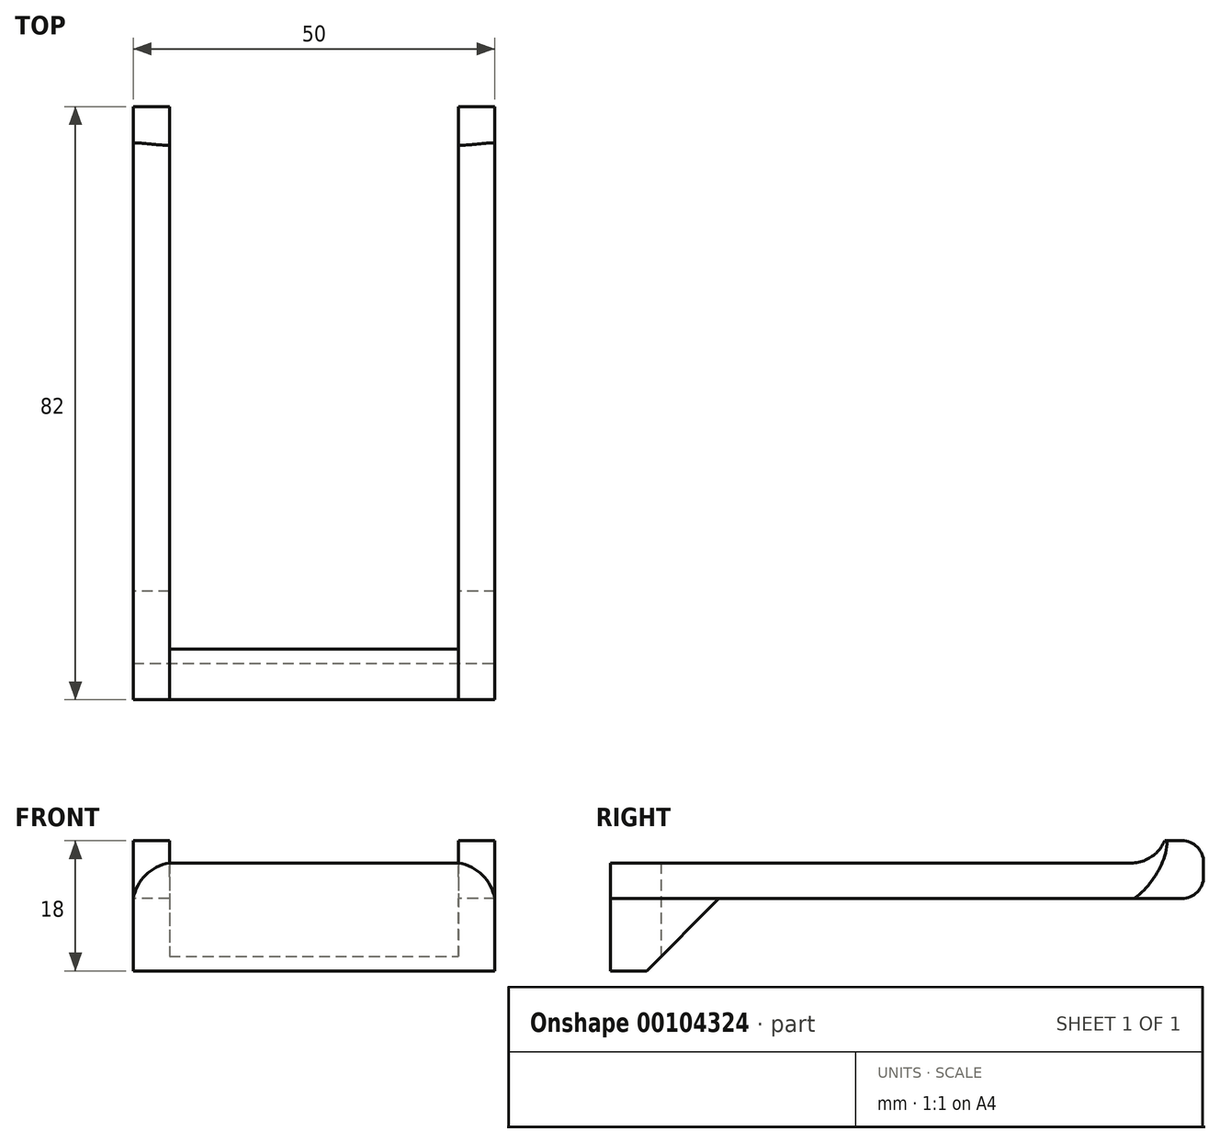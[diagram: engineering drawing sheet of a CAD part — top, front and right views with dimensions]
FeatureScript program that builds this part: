
annotation { "Feature Type Name" : "Feature", "Feature Type Description" : "" }
export const myFeature = defineFeature(function(context is Context, id is Id, definition is map)
    precondition{}
    {
        {
            var Q0;
            Q0=qCreatedBy(makeId("Front.planeOp"),FACE);
            var sketch = newSketch(context, id + "F0", { "sketchPlane" : qUnion([Q0])});
            skLineSegment(sketch, "E0.bottom", {"start": v(0, 0) * mm, "end": v(-5, 0) * mm});
            skLineSegment(sketch, "E0.top", {"start": v(0, 5) * mm, "end": v(-5, 5) * mm});
            skLineSegment(sketch, "E0.left", {"start": v(0, 0) * mm, "end": v(0, 5) * mm});
            skLineSegment(sketch, "E0.right", {"start": v(-5, 0) * mm, "end": v(-5, 5) * mm});
            skLineSegment(sketch, "E1", {"start": v(0, 5) * mm, "end": v(0, 8) * mm});
            skLineSegment(sketch, "E2", {"start": v(0, 8) * mm, "end": v(-5, 8) * mm});
            skLineSegment(sketch, "E3", {"start": v(-5, 8) * mm, "end": v(-5, 5) * mm});
            skSolve(sketch);
        }
        {
            var Q0;
            Q0=makeQuery(id+"F0.imprint","IMPRINT",FACE,{"disambiguationData":[TD([[makeQuery(id+"F0.imprint","IMPRINT",EDGE,{"derivedFrom":sQuery(id+"F0.wireOp",EDGE,"E0.bottom")}),-1.0]])]});
            extrude(context, id + "F1", {"entities" : qUnion([Q0]), "depth" : 82 * mm});
        }
        {
            var Q0;
            Q0=makeQuery(id+"F0.imprint","IMPRINT",FACE,{"disambiguationData":[TD([[makeQuery(id+"F0.imprint","IMPRINT",EDGE,{"derivedFrom":sQuery(id+"F0.wireOp",EDGE,"E0.top")}),-1.0]])]});
            extrude(context, id + "F2", {"entities" : qUnion([Q0]), "operationType" : NewBodyOperationType.ADD, "depth" : 5 * mm});
        }
        {
            var Q0;
            Q0=makeQuery(id+"F1.opExtrude","SWEPT_EDGE",EDGE,{"disambiguationData":[OSD([sQuery(id+"F0.wireOp",EDGE,"E0.top"),sQuery(id+"F0.wireOp",EDGE,"E0.right"),sQuery(id+"F0.wireOp",EDGE,"E3")])]});
            fillet(context, id + "F3", {"entities" : qUnion([Q0]), "radius" : 6.1 * mm, "tangentPropagation" : true, "allowEdgeOverflow" : false});
        }
        {
            var Q0;
            {var subQ0=sQuery(id+"F0.wireOp",EDGE,"E3");var subQ1=sQuery(id+"F0.wireOp",EDGE,"E0.top");Q0=makeQuery(id+"F3.opFillet","BLEND_EDGE",EDGE,{"blendedFrom":[makeQuery(id+"F1.opExtrude","SWEPT_EDGE",EDGE,{"disambiguationData":[OSD([subQ1,sQuery(id+"F0.wireOp",EDGE,"E0.right"),subQ0])]}),makeQuery(id+"F2.opExtrude","CAP_FACE",FACE,{"disambiguationData":[OSD([subQ1,sQuery(id+"F0.wireOp",EDGE,"E1"),sQuery(id+"F0.wireOp",EDGE,"E2"),subQ0])],"isStart":false})],"blendedInto":[makeQuery(id+"F2.opExtrude","CAP_FACE",FACE,{"disambiguationData":[OSD([subQ1,sQuery(id+"F0.wireOp",EDGE,"E1"),sQuery(id+"F0.wireOp",EDGE,"E2"),subQ0])],"isStart":false})]});}
            fillet(context, id + "F4", {"entities" : qUnion([Q0]), "radius" : 5 * mm, "tangentPropagation" : true, "allowEdgeOverflow" : false});
        }
        {
            var Q0;
            Q0=makeQuery(id+"F2.opExtrude","CAP_EDGE",EDGE,{"disambiguationData":[OSD([sQuery(id+"F0.wireOp",EDGE,"E2")])],"isStart":true});
            fillet(context, id + "F5", {"entities" : qUnion([Q0]), "radius" : 3 * mm, "tangentPropagation" : true, "allowEdgeOverflow" : false});
        }
        {
            var Q0;
            Q0=makeQuery(id+"F1.opExtrude","CAP_EDGE",EDGE,{"disambiguationData":[OSD([sQuery(id+"F0.wireOp",EDGE,"E0.bottom")])],"isStart":true});
            fillet(context, id + "F6", {"entities" : qUnion([Q0]), "radius" : 3 * mm, "tangentPropagation" : true, "allowEdgeOverflow" : false});
        }
        {
            var Q0;
            Q0=makeQuery(id+"F2.boolean.opBoolean","MERGE",FACE,{"derivedFrom":[makeQuery(id+"F1.opExtrude","SWEPT_FACE",FACE,{"disambiguationData":[OSD([sQuery(id+"F0.wireOp",EDGE,"E0.left")])]}),makeQuery(id+"F2.opExtrude","SWEPT_FACE",FACE,{"disambiguationData":[OSD([sQuery(id+"F0.wireOp",EDGE,"E1")])]})]});
            var sketch = newSketch(context, id + "F7", { "sketchPlane" : qUnion([Q0])});
            skLineSegment(sketch, "E4.bottom", {"start": v(-82, 4.92) * mm, "end": v(-75, 4.92) * mm});
            skLineSegment(sketch, "E4.top", {"start": v(-82, 0) * mm, "end": v(-75, 0) * mm});
            skLineSegment(sketch, "E4.left", {"start": v(-82, 4.92) * mm, "end": v(-82, 0) * mm});
            skLineSegment(sketch, "E4.right", {"start": v(-75, 4.92) * mm, "end": v(-75, 0) * mm});
            skSolve(sketch);
        }
        {
            var Q0;
            Q0 = qSketchRegion(id + "F7", true);
            var Q1;
            Q1=makeQuery(id+"F7.imprint","IMPRINT",FACE,{"disambiguationData":[TD([[makeQuery(id+"F7.imprint","IMPRINT",EDGE,{"derivedFrom":sQuery(id+"F7.wireOp",EDGE,"E4.bottom")}),1.0]])]});
            extrude(context, id + "F8", {"entities" : qUnion([Q0, Q1]), "operationType" : NewBodyOperationType.ADD, "depth" : 20 * mm});
        }
        {
            var Q0;
            Q0=makeQuery(id+"F1.opExtrude","SWEPT_BODY",BODY,{"disambiguationData":[OSD([sQuery(id+"F0.wireOp",EDGE,"E0.bottom"),sQuery(id+"F0.wireOp",EDGE,"E0.top"),sQuery(id+"F0.wireOp",EDGE,"E0.left"),sQuery(id+"F0.wireOp",EDGE,"E0.right")])]});
            var Q1;
            Q1=makeQuery(id+"F8.opExtrude","CAP_FACE",FACE,{"disambiguationData":[OSD([sQuery(id+"F7.wireOp",EDGE,"E4.bottom"),sQuery(id+"F7.wireOp",EDGE,"E4.top"),sQuery(id+"F7.wireOp",EDGE,"E4.left"),sQuery(id+"F7.wireOp",EDGE,"E4.right")])],"isStart":false});
            mirror(context, id + "F9", {"operationType" : NewBodyOperationType.ADD, "entities" : qUnion([Q0]), "mirrorPlane" : qUnion([Q1])});
        }
        {
            var Q0;
            {var subQ0=makeQuery(id+"F8.boolean.opBoolean","MERGE",FACE,{"derivedFrom":[makeQuery(id+"F1.opExtrude","SWEPT_FACE",FACE,{"disambiguationData":[OSD([sQuery(id+"F0.wireOp",EDGE,"E0.bottom")])]}),makeQuery(id+"F8.opExtrude","SWEPT_FACE",FACE,{"disambiguationData":[OSD([sQuery(id+"F7.wireOp",EDGE,"E4.top")])]})]});Q0=makeQuery(id+"F9.boolean.opBoolean","MERGE",FACE,{"derivedFrom":[subQ0,makeQuery(id+"F9.opPattern","COPY",FACE,{"derivedFrom":subQ0,"instanceName":"1"})]});}
            var sketch = newSketch(context, id + "F10", { "sketchPlane" : qUnion([Q0])});
            skLineSegment(sketch, "E5.bottom", {"start": v(45, 82) * mm, "end": v(-5, 82) * mm});
            skLineSegment(sketch, "E5.top", {"start": v(45, 67) * mm, "end": v(-5, 67) * mm});
            skLineSegment(sketch, "E5.left", {"start": v(45, 82) * mm, "end": v(45, 67) * mm});
            skLineSegment(sketch, "E5.right", {"start": v(-5, 82) * mm, "end": v(-5, 67) * mm});
            skSolve(sketch);
        }
        {
            var Q0;
            Q0=makeQuery(id+"F10.imprint","IMPRINT",FACE,{"disambiguationData":[TD([[makeQuery(id+"F10.imprint","IMPRINT",EDGE,{"derivedFrom":sQuery(id+"F10.wireOp",EDGE,"E5.bottom")}),1.0]])]});
            extrude(context, id + "F11", {"entities" : qUnion([Q0]), "operationType" : NewBodyOperationType.ADD, "depth" : 10 * mm});
        }
        {
            var Q0;
            {var subQ0=sQuery(id+"F10.wireOp",EDGE,"E5.top");var subQ1=sQuery(id+"F0.wireOp",EDGE,"E0.bottom");Q0=makeQuery(id+"F11.opExtrude","CAP_EDGE",EDGE,{"disambiguationData":[OSD([subQ0]),TDD([makeQuery(id+"F10.imprint","IMPRINT",EDGE,{"disambiguationData":[TD([[makeQuery(id+"F10.imprint","INTERSECT",VERTEX,{"derivedFrom":[makeQuery(id+"F9.opPattern","COPY",EDGE,{"derivedFrom":makeQuery(id+"F1.opExtrude","SWEPT_EDGE",EDGE,{"disambiguationData":[OSD([subQ1,sQuery(id+"F0.wireOp",EDGE,"E0.left")])]}),"instanceName":"1"}),subQ0]}),1.0]])],"derivedFrom":subQ0})])],"isStart":false});}
            var Q1;
            {var subQ0=sQuery(id+"F10.wireOp",EDGE,"E5.top");var subQ1=sQuery(id+"F0.wireOp",EDGE,"E0.bottom");Q1=makeQuery(id+"F11.opExtrude","CAP_EDGE",EDGE,{"disambiguationData":[OSD([subQ0]),TDD([makeQuery(id+"F10.imprint","IMPRINT",EDGE,{"disambiguationData":[TD([[makeQuery(id+"F10.imprint","INTERSECT",VERTEX,{"derivedFrom":[makeQuery(id+"F1.opExtrude","SWEPT_EDGE",EDGE,{"disambiguationData":[OSD([subQ1,sQuery(id+"F0.wireOp",EDGE,"E0.left")])]}),subQ0]}),-1.0]])],"derivedFrom":subQ0})])],"isStart":false});}
            chamfer(context, id + "F12", {"entities" : qUnion([Q0, Q1]), "width" : 10 * mm, "tangentPropagation" : true});
        }
        {
            var Q0;
            Q0=makeQuery(id+"F1.opExtrude","SWEPT_BODY",BODY,{"disambiguationData":[OSD([sQuery(id+"F0.wireOp",EDGE,"E0.bottom"),sQuery(id+"F0.wireOp",EDGE,"E0.top"),sQuery(id+"F0.wireOp",EDGE,"E0.left"),sQuery(id+"F0.wireOp",EDGE,"E0.right")])]});
            transform(context, id + "F13", {"entities" : qUnion([Q0]), "transformType" : TransformType.TRANSLATION_3D, "dx" : -20 * mm, "dy" : 82 * mm, "dz" : 85 * mm, "makeCopy" : false});
        }
    });
